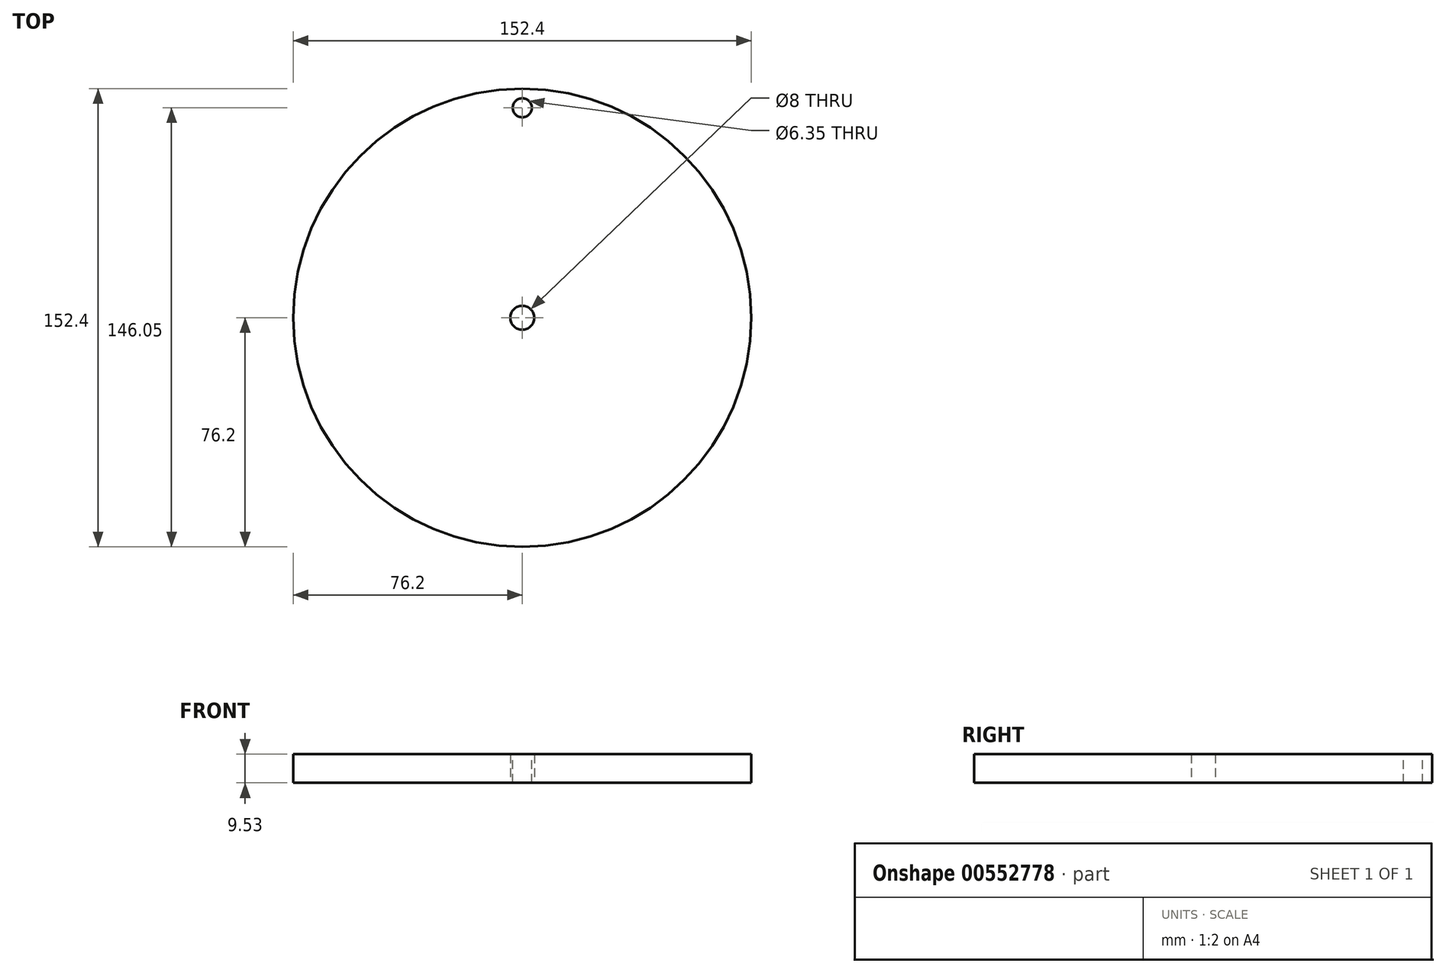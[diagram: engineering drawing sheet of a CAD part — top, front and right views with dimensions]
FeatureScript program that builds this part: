
annotation { "Feature Type Name" : "Feature", "Feature Type Description" : "" }
export const myFeature = defineFeature(function(context is Context, id is Id, definition is map)
    precondition{}
    {
        {
            var Q0;
            Q0=qCreatedBy(makeId("Top.planeOp"),FACE);
            var sketch = newSketch(context, id + "F0", { "sketchPlane" : qUnion([Q0])});
            skCircle(sketch, "E0", {"center": v(0, 0) * mm, "radius": 76.2 * mm});
            skCircle(sketch, "E1", {"center": v(0, 0) * mm, "radius": 4 * mm});
            skSolve(sketch);
        }
        {
            var Q0;
            Q0 = qSketchRegion(id + "F0", true);
            extrude(context, id + "F1", {"entities" : qUnion([Q0]), "depth" : 9.52 * mm, "offsetDistance" : 25.4 * mm});
        }
        {
            var Q0;
            Q0=makeQuery(id+"F1.opExtrude","CAP_FACE",FACE,{"disambiguationData":[OSD([sQuery(id+"F0.wireOp",EDGE,"E0"),sQuery(id+"F0.wireOp",EDGE,"E1")])],"isStart":false});
            var sketch = newSketch(context, id + "F2", { "sketchPlane" : qUnion([Q0])});
            skCircle(sketch, "E2", {"center": v(0, 69.85) * mm, "radius": 3.18 * mm});
            skSolve(sketch);
        }
        {
            var Q0;
            Q0=sQuery(id+"F2.wireOp",VERTEX,"E2.center");
            var Q1;
            Q1=makeQuery(id+"F1.opExtrude","SWEPT_BODY",BODY,{"disambiguationData":[OSD([sQuery(id+"F0.wireOp",EDGE,"E0"),sQuery(id+"F0.wireOp",EDGE,"E1")])]});
            hole(context, id + "F3", {"style" : HoleStyle.SIMPLE, "endStyle" : HoleEndStyle.THROUGH, "holeDiameter" : 6.35 * mm, "isTappedThrough" : true, "tappedDepth" : 12.7 * mm, "tapClearance" : 3, "locations" : qUnion([Q0]), "scope" : qUnion([Q1])});
        }
    });
